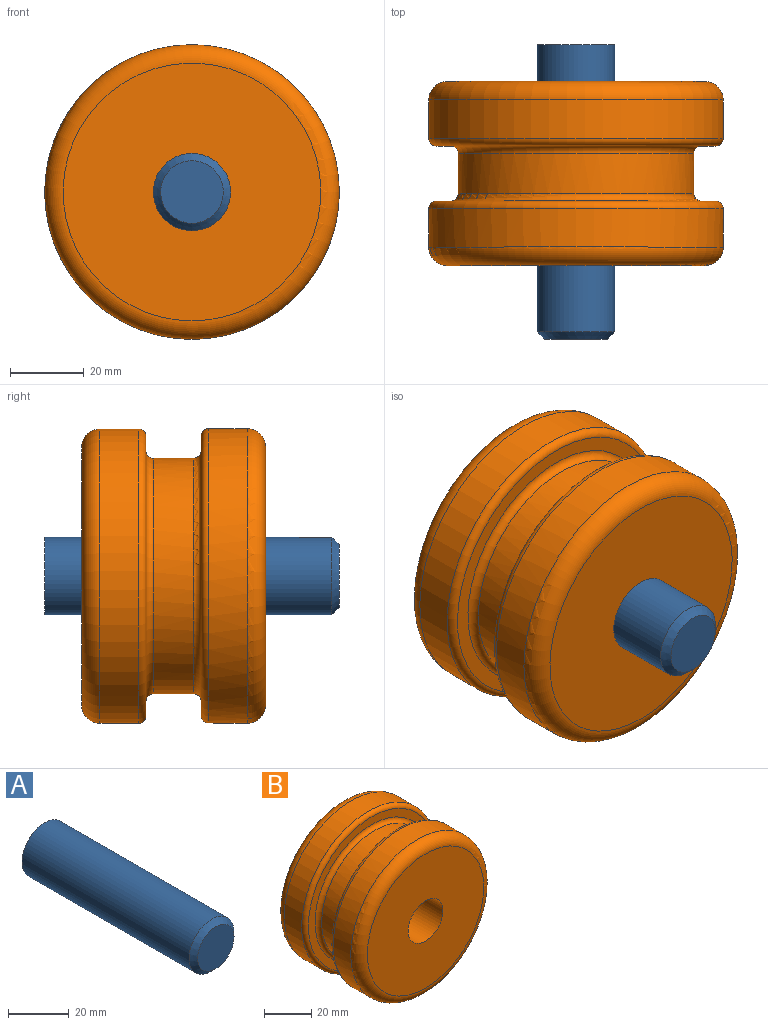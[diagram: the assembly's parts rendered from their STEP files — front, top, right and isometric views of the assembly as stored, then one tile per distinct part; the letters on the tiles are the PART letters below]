
ASSEMBLY  parts=2 mates=1
PART A: 4 faces, bbox 21x80x21 mm
  f0: cylinder r=10.5mm len=78mm, axis (0,1,0), area 5145.9mm2, adj f2,f3
  f1: plane 17x17mm, normal (0,-1,0), area 227mm2, adj f3
  f2: plane 21x21mm, normal (0,1,0), area 346.4mm2, adj f0
  f3: cone r=8.5mm half-angle=45deg, axis (0,1,0), area 168.8mm2, adj f0,f1
PART B: 14 faces, bbox 86.6x50x86.6 mm
  f0: cylinder r=40mm len=80mm, axis (0,1,0), area 2638.9mm2, adj f6,f10
  f1: cylinder r=40mm len=80mm, axis (0,1,0), area 2638.9mm2, adj f5,f13
  f2: cylinder r=10.5mm len=50mm, axis (0,1,0), area 3298.7mm2, adj f3,f4
  f3: plane 70x70mm, normal (0,-1,0), area 3502.1mm2, adj f2,f6
  f4: plane 70x70mm, normal (0,1,0), area 3502.1mm2, adj f2,f5
  f5: torus R=35mm, axis (0,-1,0), area 1884.3mm2, adj f1,f4
  f6: torus R=35mm, axis (0,-1,0), area 1884.3mm2, adj f0,f3
  f7: plane 76x76mm, normal (0,1,0), area 904.8mm2, adj f10,f11
  f8: cylinder r=32mm len=64mm, axis (0,-1,0), area 2211.7mm2, adj f11,f12
  f9: plane 76x76mm, normal (0,-1,0), area 904.8mm2, adj f12,f13
  f10: torus R=38mm, axis (0,1,0), area 775.2mm2, adj f0,f7
  f11: torus R=34mm, axis (0,1,0), area 646mm2, adj f7,f8
  f12: torus R=34mm, axis (0,-1,0), area 646mm2, adj f8,f9
  f13: torus R=38mm, axis (0,-1,0), area 775.2mm2, adj f1,f9
PLACE A t=(-16.52,23.12,-3.5)mm
PLACE B t=(-16.52,13.12,-3.5)mm
MATE revolute A.f0 <-> B.f2  axis (0,1,0) through (-16.52,23.12,-3.5)mm
